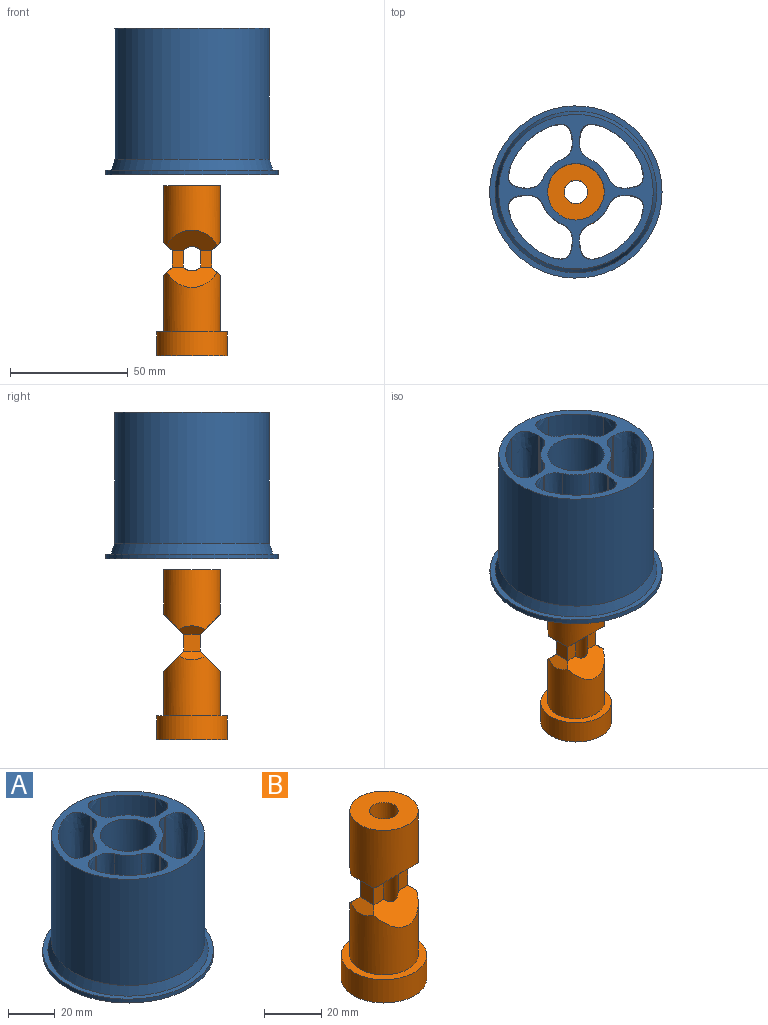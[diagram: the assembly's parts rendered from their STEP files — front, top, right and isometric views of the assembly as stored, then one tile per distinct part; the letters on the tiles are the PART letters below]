
ASSEMBLY  parts=2 mates=1
PART A: 39 faces, bbox 73x73x68.2 mm
  f0: cylinder r=29.75mm len=62mm, axis (0,0,-1), area 1484.8mm2, adj f5,f8,f24,f28
  f1: cylinder r=29.75mm len=62mm, axis (0,0,-1), area 1484.8mm2, adj f5,f8,f26,f27
  f2: cylinder r=29.75mm len=62mm, axis (0,0,-1), area 1484.8mm2, adj f5,f8,f23,f30
  f3: cylinder r=29.75mm len=62mm, axis (0,0,-1), area 1484.8mm2, adj f5,f8,f25,f29
  f4: cylinder r=32.75mm len=65.5mm, axis (0,0,-1), area 11420.5mm2, adj f5,f9
  f5: plane 65.5x65.5mm, normal (0,0,1), area 1142.6mm2, adj f0,f1,f2,f3,f4,f10,f11,f12
  f6: cylinder r=36.5mm len=73mm, axis (0,0,-1), area 458.7mm2, adj f7,f8
  f7: plane 73x73mm, normal (0,0,1), area 500.1mm2, adj f6,f9
  f8: plane 73x73mm, normal (0,0,-1), area 1958.4mm2, adj f0,f1,f2,f3,f6,f10,f11,f12
  f9: cone r=32.75mm half-angle=18.4deg, axis (0,0,-1), area 998.4mm2, adj f4,f7
  f10: plane 62x0.81mm, normal (1,0,0), area 50.3mm2, adj f5,f8,f30,f38
  f11: plane 62x0.81mm, normal (-1,0,0), area 50.3mm2, adj f5,f8,f28,f36
  f12: cylinder r=15mm len=62mm, axis (0,0,-1), area 723mm2, adj f5,f8,f35,f36
  f13: plane 62x0.81mm, normal (0,1,0), area 50.3mm2, adj f5,f8,f24,f35
  f14: plane 62x0.81mm, normal (0,-1,0), area 50.3mm2, adj f5,f8,f26,f34
  f15: cylinder r=15mm len=62mm, axis (0,0,-1), area 723mm2, adj f5,f8,f33,f34
  f16: plane 62x0.81mm, normal (-1,0,0), area 50.3mm2, adj f5,f8,f27,f33
  f17: plane 62x0.81mm, normal (1,0,0), area 50.3mm2, adj f5,f8,f29,f32
  f18: cylinder r=15mm len=62mm, axis (0,0,-1), area 723mm2, adj f5,f8,f31,f32
  f19: plane 62x0.81mm, normal (0,-1,0), area 50.3mm2, adj f5,f8,f25,f31
  f20: plane 62x0.81mm, normal (0,1,0), area 50.3mm2, adj f5,f8,f23,f37
  f21: cylinder r=15mm len=62mm, axis (0,0,-1), area 723mm2, adj f5,f8,f37,f38
  f22: cylinder r=12mm len=62mm, axis (0,0,-1), area 4674.7mm2, adj f5,f8
  f23: bspline ~68.2x10.37mm, area 930.3mm2, adj f2,f5,f8,f20
  f24: bspline ~68.2x10.37mm, area 930.3mm2, adj f0,f5,f8,f13
  f25: bspline ~68.2x10.37mm, area 930.3mm2, adj f3,f5,f8,f19
  f26: bspline ~68.2x10.37mm, area 930.3mm2, adj f1,f5,f8,f14
  f27: bspline ~68.2x10.37mm, area 930.3mm2, adj f1,f5,f8,f16
  f28: bspline ~68.2x10.37mm, area 930.3mm2, adj f0,f5,f8,f11
  f29: bspline ~68.2x10.37mm, area 930.3mm2, adj f3,f5,f8,f17
  f30: bspline ~68.2x10.37mm, area 930.3mm2, adj f2,f5,f8,f10
  f31: bspline ~68.2x6.46mm, area 514.2mm2, adj f5,f8,f18,f19
  f32: bspline ~68.2x6.46mm, area 514.2mm2, adj f5,f8,f17,f18
  f33: bspline ~68.2x6.46mm, area 514.2mm2, adj f5,f8,f15,f16
  f34: bspline ~68.2x6.46mm, area 514.2mm2, adj f5,f8,f14,f15
  f35: bspline ~68.2x6.46mm, area 514.2mm2, adj f5,f8,f12,f13
  f36: bspline ~68.2x6.46mm, area 514.2mm2, adj f5,f8,f11,f12
  f37: bspline ~68.2x6.46mm, area 514.2mm2, adj f5,f8,f20,f21
  f38: bspline ~68.2x6.46mm, area 514.2mm2, adj f5,f8,f10,f21
PART B: 21 faces, bbox 30x30x72 mm
  f0: cylinder r=12mm len=25.25mm, axis (0,0,-1), area 1664.9mm2, adj f2,f4,f9,f15,f18
  f1: cylinder r=12mm len=25.25mm, axis (0,0,-1), area 1664.9mm2, adj f3,f5,f6,f16,f19
  f2: plane 21.22x8.61mm, normal (0,0.71,0.71), area 184.7mm2, adj f0,f10,f11,f12,f15,f18
  f3: plane 21.22x8.61mm, normal (0,0.71,-0.71), area 184.7mm2, adj f1,f10,f11,f12,f16,f19
  f4: plane 21.22x8.61mm, normal (0,-0.71,0.71), area 184.7mm2, adj f0,f10,f13,f14,f15,f18
  f5: plane 21.22x8.61mm, normal (0,-0.71,-0.71), area 184.7mm2, adj f1,f10,f13,f14,f16,f19
  f6: plane 24x24mm, normal (0,0,1), area 373.8mm2, adj f1,f10
  f7: cylinder r=15mm len=30mm, axis (0,0,1), area 942.5mm2, adj f8,f9
  f8: plane 30x30mm, normal (0,0,-1), area 628.3mm2, adj f7,f10
  f9: plane 30x30mm, normal (0,0,1), area 254.5mm2, adj f0,f7
  f10: cylinder r=5mm len=72mm, axis (0,0,-1), area 2110.4mm2, adj f2,f3,f4,f5,f6,f8,f11,f12
  f11: plane 7.07x4.72mm, normal (0,1,0), area 33.4mm2, adj f2,f3,f10,f17
  f12: plane 7.07x4.72mm, normal (0,1,0), area 33.4mm2, adj f2,f3,f10,f20
  f13: plane 7.07x4.72mm, normal (0,-1,0), area 33.4mm2, adj f4,f5,f10,f20
  f14: plane 7.07x4.72mm, normal (0,-1,0), area 33.4mm2, adj f4,f5,f10,f17
  f15: plane 11.22x3.61mm, normal (0.71,0,0.71), area 43.1mm2, adj f0,f2,f4,f17
  f16: plane 11.22x3.61mm, normal (0.71,0,-0.71), area 43.1mm2, adj f1,f3,f5,f17
  f17: plane 7.07x6.79mm, normal (1,0,0), area 48mm2, adj f11,f14,f15,f16
  f18: plane 11.22x3.61mm, normal (-0.71,0,0.71), area 43.1mm2, adj f0,f2,f4,f20
  f19: plane 11.22x3.61mm, normal (-0.71,0,-0.71), area 43.1mm2, adj f1,f3,f5,f20
  f20: plane 7.07x6.79mm, normal (-1,0,0), area 48mm2, adj f12,f13,f18,f19
PLACE A t=(-24.17,1.58,-7.7)mm fixed
PLACE B t=(-24.17,1.58,-74.28)mm
MATE slider B.f0 <-> A.f22  axis (0,0,1) through (-24.17,1.58,-12.28)mm
